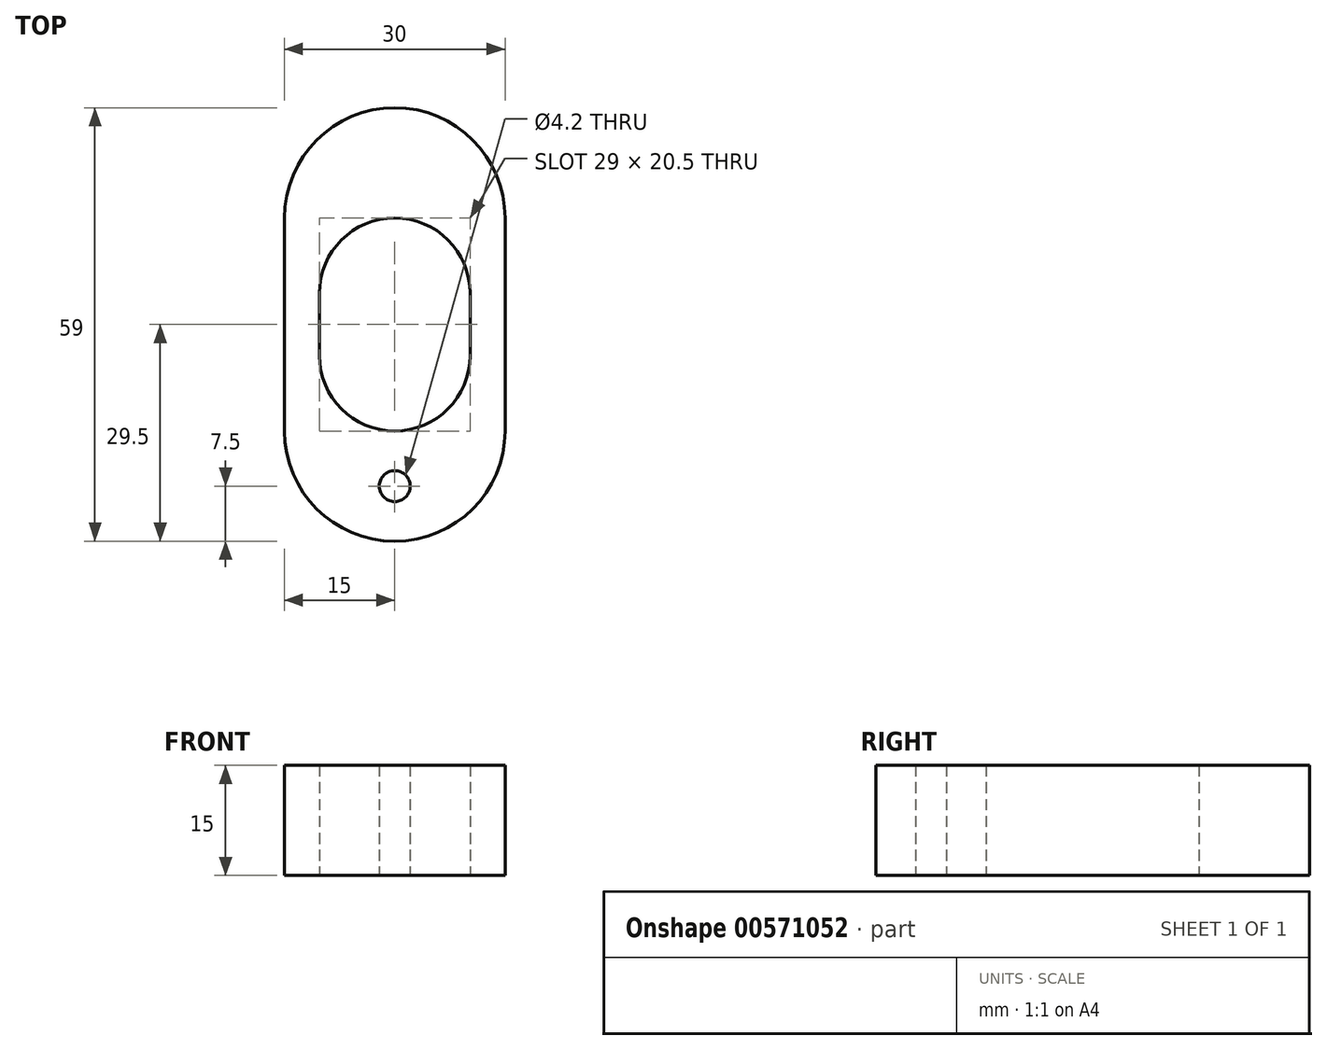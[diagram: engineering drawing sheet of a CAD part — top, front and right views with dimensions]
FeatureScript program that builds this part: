
annotation { "Feature Type Name" : "Feature", "Feature Type Description" : "" }
export const myFeature = defineFeature(function(context is Context, id is Id, definition is map)
    precondition{}
    {
        {
            var Q0;
            Q0=qCreatedBy(makeId("Top.planeOp"),FACE);
            var sketch = newSketch(context, id + "F0", { "sketchPlane" : qUnion([Q0])});
            skArc(sketch, "E0", {"start": v(15, 14.5) * mm, "mid": v(0, 29.5) * mm, "end": v(-15, 14.5) * mm});
            skLineSegment(sketch, "E1", {"start": v(-6.83, 0) * mm, "end": v(9.6, 0) * mm, "construction": true});
            skCircle(sketch, "E2", {"center": v(0, 22) * mm, "radius": 2.1 * mm});
            skArc(sketch, "E3", {"start": v(10.25, 4.25) * mm, "mid": v(0, 14.5) * mm, "end": v(-10.25, 4.25) * mm});
            skArc(sketch, "E4.MirrorC", {"start": v(10.25, -4.25) * mm, "mid": v(0, -14.5) * mm, "end": v(-10.25, -4.25) * mm});
            skCircle(sketch, "E5.MirrorC", {"center": v(0, -22) * mm, "radius": 2.1 * mm});
            skLineSegment(sketch, "E6", {"start": v(-10.25, 4.25) * mm, "end": v(-10.25, -4.25) * mm});
            skLineSegment(sketch, "E7", {"start": v(10.25, 4.25) * mm, "end": v(10.25, -4.25) * mm});
            skLineSegment(sketch, "E8", {"start": v(-15, 14.5) * mm, "end": v(-15, -14.5) * mm});
            skLineSegment(sketch, "E9", {"start": v(15, 14.5) * mm, "end": v(15, -14.5) * mm});
            skArc(sketch, "E10.trimOffspring", {"start": v(15, -14.5) * mm, "mid": v(0, -29.5) * mm, "end": v(-15, -14.5) * mm});
            skSolve(sketch);
        }
        {
            var Q0;
            Q0=makeQuery(id+"F0.imprint","IMPRINT",FACE,{"disambiguationData":[TD([[makeQuery(id+"F0.imprint","IMPRINT",EDGE,{"derivedFrom":sQuery(id+"F0.wireOp",EDGE,"E0")}),1.0]])]});
            extrude(context, id + "F1", {"entities" : qUnion([Q0]), "depth" : 5 * mm, "offsetDistance" : 25 * mm});
        }
        {
            var Q0;
            Q0=makeQuery(id+"F0.imprint","IMPRINT",FACE,{"disambiguationData":[TD([[makeQuery(id+"F0.imprint","IMPRINT",EDGE,{"derivedFrom":sQuery(id+"F0.wireOp",EDGE,"E2")}),1.0]])]});
            var Q1;
            Q1=makeQuery(id+"F0.imprint","IMPRINT",FACE,{"disambiguationData":[TD([[makeQuery(id+"F0.imprint","IMPRINT",EDGE,{"derivedFrom":sQuery(id+"F0.wireOp",EDGE,"E5.MirrorC")}),-1.0]])]});
            extrude(context, id + "F2", {"entities" : qUnion([Q0, Q1]), "operationType" : NewBodyOperationType.ADD, "depth" : 15 * mm, "offsetDistance" : 25 * mm});
        }
    });
